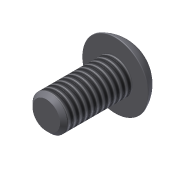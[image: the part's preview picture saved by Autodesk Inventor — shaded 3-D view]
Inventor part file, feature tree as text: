
AUTODESK INVENTOR PART (.ipt)
format: ipt  version: 2013 (Build 170138000, 138)  size: 134,144 bytes
history: native  units: in
note: dims shown in document units (in); Inventor stores cm internally (conversion verified against a paired STEP export)
features: sketch x3, extrude x2, revolve x1, chamfer x1, thread x1
ambient origin geometry x8: Origin, YZ Plane, XZ Plane, XY Plane, X Axis, Y Axis, Z Axis, Center Point
bodies: Solid1 (feature_tree)
feature tree (8):
  extrude  "Extrusion1"  Depth=0.375in TaperAngle=0.0deg
  revolve  "Revolution1"  [1 undecoded]
  extrude  "Extrusion2"  Depth=0.125in
  chamfer  "Chamfer1"  Distance=0.0625in
  thread  "Thread1"  [1 undecoded]
  sketch  "Sketch1"  dims[d0=0.19in d1=0.375in d2=0.0in]
  sketch  "Sketch2"  dims[d3=0.101in d6=0.08in]
  sketch  "Sketch3"  dims[d7=90.0deg d8=0.125in d9=0.0625in d10=0.0in d12=0.1805in d13=0.02in d14=0.125in d15=45.0deg d16=1.0in d17=0.0in d18=0.003in]
note: 2 required parameter values undecoded (feature->parameter linkage not recoverable at this tier; creation-order binding heuristic only, values carry confidence <= 0.55)